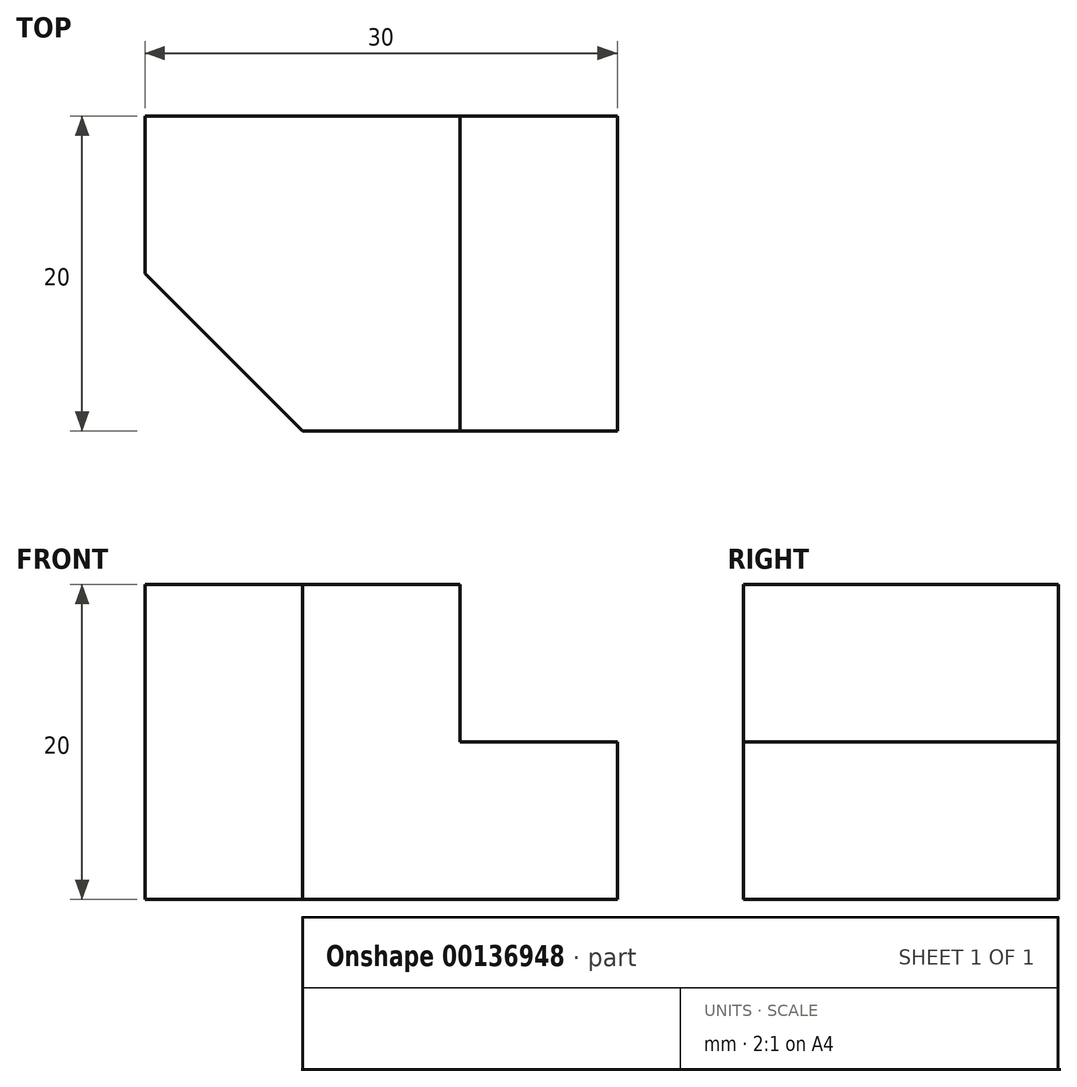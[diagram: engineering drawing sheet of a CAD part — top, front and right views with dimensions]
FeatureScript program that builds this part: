
annotation { "Feature Type Name" : "Feature", "Feature Type Description" : "" }
export const myFeature = defineFeature(function(context is Context, id is Id, definition is map)
    precondition{}
    {
        {
            var Q0;
            Q0=qCreatedBy(makeId("Front.planeOp"),FACE);
            var sketch = newSketch(context, id + "F0", { "sketchPlane" : qUnion([Q0])});
            skLineSegment(sketch, "E0.bottom", {"start": v(0, 0) * mm, "end": v(30, 0) * mm});
            skLineSegment(sketch, "E0.top", {"start": v(0, 20) * mm, "end": v(30, 20) * mm});
            skLineSegment(sketch, "E0.left", {"start": v(0, 0) * mm, "end": v(0, 20) * mm});
            skLineSegment(sketch, "E0.right", {"start": v(30, 0) * mm, "end": v(30, 20) * mm});
            skLineSegment(sketch, "E1.bottom", {"start": v(20, 20) * mm, "end": v(30, 20) * mm});
            skLineSegment(sketch, "E1.top", {"start": v(20, 10) * mm, "end": v(30, 10) * mm});
            skLineSegment(sketch, "E1.left", {"start": v(20, 20) * mm, "end": v(20, 10) * mm});
            skLineSegment(sketch, "E1.right", {"start": v(30, 20) * mm, "end": v(30, 10) * mm});
            skSolve(sketch);
        }
        {
            var Q0;
            Q0=makeQuery(id+"F0.imprint","IMPRINT",FACE,{"disambiguationData":[TD([[makeQuery(id+"F0.imprint","IMPRINT",EDGE,{"derivedFrom":sQuery(id+"F0.wireOp",EDGE,"E0.bottom")}),1.0]])]});
            extrude(context, id + "F1", {"entities" : qUnion([Q0]), "depth" : 20 * mm});
        }
        {
            var Q0;
            Q0=makeQuery(id+"F1.opExtrude","SWEPT_FACE",FACE,{"disambiguationData":[OSD([sQuery(id+"F0.wireOp",EDGE,"E0.top")])]});
            var sketch = newSketch(context, id + "F2", { "sketchPlane" : qUnion([Q0])});
            skLineSegment(sketch, "E2", {"start": v(0, -10) * mm, "end": v(10, -20) * mm});
            skSolve(sketch);
        }
        {
            var Q0;
            {var subQ0=sQuery(id+"F2.wireOp",EDGE,"E2");Q0=makeQuery(id+"F2.imprint","IMPRINT",FACE,{"disambiguationData":[TD([[makeQuery(id+"F2.imprint","IMPRINT",EDGE,{"derivedFrom":subQ0}),-1.0]])]});}
            extrude(context, id + "F3", {"entities" : qUnion([Q0]), "operationType" : NewBodyOperationType.REMOVE, "endBound" : BoundingType.THROUGH_ALL, "oppositeDirection" : true, "depth" : 25 * mm});
        }
    });
